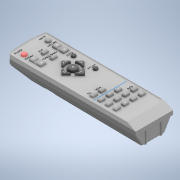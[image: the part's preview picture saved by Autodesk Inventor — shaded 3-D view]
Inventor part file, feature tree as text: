
AUTODESK INVENTOR PART (.ipt)
format: ipt  version: 2020 (Build 240168000, 168)  size: 3,860,992 bytes
history: native  units: mm
features: fillet x30, extrude x27, sketch x27, other x20, projected_geometry x15, chamfer x2
ambient origin geometry x8: Origin, YZ Plane, XZ Plane, XY Plane, X Axis, Y Axis, Z Axis, Center Point
bodies: Body1 (feature_tree)
feature tree (121):
  other  "Bryła1"
  extrude  "Wyciągnięcie proste1"  Depth=25.0mm
  chamfer  "Faza1"  Distance=20.0mm
  chamfer  "Faza2"  Distance=44.0mm
  sketch  "Szkic4"
  extrude  "Wyciągnięcie proste2"  Depth=10.0mm TaperAngle=45.0deg
  fillet  "Zaokrąglenie1"  Radius=25.0mm
  extrude  "Wyciągnięcie proste3"  Depth=1.0mm
  fillet  "Zaokrąglenie2"  Radius=2.0mm
  extrude  "Wyciągnięcie proste4"  Depth=1.0mm
  other  "Płaszczyzna konstrukcyjna1"
  extrude  "Wyciągnięcie proste6"  Depth=2.0mm
  other  "Płaszczyzna konstrukcyjna2"
  extrude  "Wyciągnięcie proste7"  TaperAngle=90.0deg  [1 undecoded]
  other  "Pochylenie ściany1"
  other  "Edytuj bezpośrednio1"
  other  "Edytuj bezpośrednio2"
  extrude  "Wyciągnięcie proste8"  Depth=20.0mm
  fillet  "Zaokrąglenie4"  Radius=7.0mm
  fillet  "Zaokrąglenie5"  Radius=12.0mm
  fillet  "Zaokrąglenie7"  Radius=12.0mm
  fillet  "Zaokrąglenie8"  Radius=10.0mm
  fillet  "Zaokrąglenie9"  Radius=1.5mm
  fillet  "Zaokrąglenie10"  Radius=1.5mm
  extrude  "Wyciągnięcie proste9"  Depth=3.0mm TaperAngle=0.0deg
  extrude  "Wyciągnięcie proste10"  Depth=3.5mm
  fillet  "Zaokrąglenie11"  [1 undecoded]
  fillet  "Zaokrąglenie12"  Radius=3.0mm
  extrude  "Wyciągnięcie proste11"  Depth=1.0mm
  other  "Edytuj bezpośrednio3"
  extrude  "Wyciągnięcie proste12"  Depth=3.0mm
  fillet  "Zaokrąglenie13"  Radius=0.5mm
  fillet  "Zaokrąglenie14"  [1 undecoded]
  extrude  "Wyciągnięcie proste13"  Depth=0.2mm
  extrude  "Wyciągnięcie proste14"  Depth=0.2mm
  extrude  "Wyciągnięcie proste15"  Depth=0.2mm
  fillet  "Zaokrąglenie15"  Radius=0.1mm
  extrude  "Wyciągnięcie proste16"  [1 undecoded]
  fillet  "Zaokrąglenie16"  Radius=0.1mm
  fillet  "Zaokrąglenie17"  Radius=9.55mm
  extrude  "Wyciągnięcie proste17"  [1 undecoded]
  fillet  "Zaokrąglenie18"  [1 undecoded]
  extrude  "Wyciągnięcie proste18"  Depth=0.1mm TaperAngle=0.0deg
  other  "Edytuj bezpośrednio4"
  fillet  "Zaokrąglenie19"  Radius=43.8mm
  extrude  "Wyciągnięcie proste19"  Depth=2.0mm
  fillet  "Zaokrąglenie20"  Radius=11.9mm
  extrude  "Wyciągnięcie proste20"  Depth=2.0mm
  fillet  "Zaokrąglenie21"  Radius=14.916887mm
  extrude  "Wyciągnięcie proste21"  Depth=14.916887mm
  fillet  "Zaokrąglenie22"  Radius=11.9mm
  other  "Edytuj bezpośrednio5"
  fillet  "Zaokrąglenie23"  Radius=0.7mm
  extrude  "Wyciągnięcie proste22"  Depth=0.3mm
  other  "Edytuj bezpośrednio6"
  fillet  "Zaokrąglenie24"  Radius=2.0mm
  extrude  "Wyciągnięcie proste23"  Depth=2.0mm
  other  "Edytuj bezpośrednio7"
  fillet  "Zaokrąglenie25"  Radius=2.0mm
  fillet  "Zaokrąglenie26"  Radius=2.0mm
  fillet  "Zaokrąglenie27"  Radius=0.8mm
  fillet  "Zaokrąglenie29"  Radius=54.0mm
  fillet  "Zaokrąglenie30"  Radius=21.0mm
  fillet  "Zaokrąglenie31"  Radius=1.672mm
  fillet  "Zaokrąglenie32"  Radius=1.671797mm
  extrude  "Wyciągnięcie proste24"  Depth=7.0mm
  fillet  "Zaokrąglenie33"  Radius=1.5mm
  extrude  "Wyciągnięcie proste25"  Depth=0.3mm
  extrude  "Wyciągnięcie proste26"  Depth=1.0mm TaperAngle=0.0deg
  extrude  "Wyciągnięcie proste27"  Depth=13.0mm
  extrude  "Wyciągnięcie proste28"  Depth=15.0mm
  sketch  "Szkic2"
  sketch  "Szkic5"
  projected_geometry  "Pętla rzutowana1"
  sketch  "Szkic6"
  projected_geometry  "Pętla rzutowana2"
  sketch  "Szkic8"
  sketch  "Szkic9"
  sketch  "Szkic10"
  projected_geometry  "Pętla rzutowana4"
  sketch  "Szkic11"
  projected_geometry  "Pętla rzutowana5"
  sketch  "Szkic12"
  sketch  "Szkic14"
  sketch  "Szkic15"
  sketch  "Szkic16"
  sketch  "Szkic17"
  projected_geometry  "Pętla rzutowana6"
  sketch  "Szkic19"
  projected_geometry  "Pętla rzutowana7"
  sketch  "Szkic20"
  projected_geometry  "Pętla rzutowana8"
  sketch  "Szkic21"
  projected_geometry  "Pętla rzutowana9"
  sketch  "Szkic22"
  projected_geometry  "Pętla rzutowana10"
  sketch  "Szkic24"
  sketch  "Szkic26"
  sketch  "Szkic27"
  sketch  "Szkic28"
  projected_geometry  "Pętla rzutowana11"
  sketch  "Szkic29"
  sketch  "Szkic30"
  projected_geometry  "Pętla rzutowana12"
  sketch  "Szkic32"
  sketch  "Szkic33"
  sketch  "Szkic34"
  projected_geometry  "Pętla rzutowana13"
  sketch  "Szkic35"
  projected_geometry  "Pętla rzutowana14"
  projected_geometry  "Pętla rzutowana15"
  projected_geometry  "Pętla rzutowana16"
  other  "Przesuń1"
  other  "Przesuń2"
  other  "Przesuń3"
  other  "Przesuń4"
  other  "Przesuń5"
  other  "Rozmiar1"
  other  "Rozmiar2"
  other  "Rozmiar3"
  other  "Rozmiar4"
note: 6 required parameter values undecoded (feature->parameter linkage not recoverable at this tier; creation-order binding heuristic only, values carry confidence <= 0.55)
